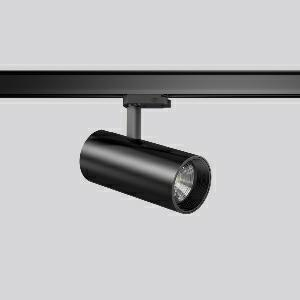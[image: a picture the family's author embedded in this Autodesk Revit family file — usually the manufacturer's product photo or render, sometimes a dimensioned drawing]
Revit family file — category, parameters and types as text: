
# Revit family: deecos_s_mini_742208_003_1_4eb7
name_source: partatom
category: Lighting Fixtures
units: mm (PartAtom-declared; Revit-internal decimal feet)

## family parameters
Cut with Voids When Loaded = No
Host = Face
Light Source = No
Part Type = Normal
Room Calculation Point = No
Round Connector Dimension = Use Diameter
Shared = No

## types (1)
- DEECOS S mini (1 x LED Modul 940, 3000 lm, 4000)
    Apparent Load = 29 VA
    Approval mark = CE
    CIE Flux Codes = 98 100 100 100 100
    Color Rendering = 92
    Color Temperature = 4000
    Default Elevation = 1800 mm
    Description = Series: DEECOS S mini
LED surface-mounted projector in modern design with no visible cooling ribs. Housing: die-cast aluminium, powder-coated. Rotation range: 356°. Swivel range: 90°. Black plastic ring and recessed LED to prevent glare from the side. Optical assembly with lens made of plastic (polycarbonate) for the best homogeneous light distribution - can be changed without tools. Best colour rendering index Ra>90. With multi adaptor for 3-circuit tracks 230 V. Suitable for Track on ceiling, Wall track. High quality converter without flickering and stroboscopic effect. The following accessories can be mounted without use of tools: interchangeable lenses, decorative glasses, honeycomb louvre, clear and frosted diffusers, white interchangeable plastic ring. 
Colour: deep black, matt (RAL 9005)
Diameter: 87 mm
Height: 214 mm
Lamp: LED
Socket: without socket
Colour temperature: 4000K
Colour rendering index (CRI): 92
System power: 29 W
Rated luminous flux: 3000 lm
Luminous efficiency: 103 lm/W
Control gear: Regulated power supply
Protection class: I
Type of protection: IP 20
    Height = 214 mm
    Lamp = 1 x LED Modul 940
    Lamp Light Flux = 3000 lm
    Lamp count = 1
    Length = 87 mm
    Lifetime = 50000 h
    Luminous efficacy = 103 lm/W
    Manufacturer = RZB
    ModVariant = No
    Model = 742208.003.1
    Mounting Place = Ceiling
    Mounting Type = Rail mounted
    Number of Poles = 1
    OnlyDefault = Yes
    Power Factor = 1
    Product Name = DEECOS S mini
    Product group = Track mounted projectors
    ProductGroupID = 301
    Protection Class = Protection class I
    Protection Degree = IP 20
    RLX_Detail_Level = 1
    RLX_Emergency_Light_Flux = 0 lm
    RLX_Emergency_Type = 0
    RLX_Emergency_Type_DB = No
    RlxData = <blob elided: 38793 chars, md5=b47558ec>
    Socket = socket
    Standby Power = 0 W
    System Light Flux = 3000 lm
    System Power = 29 W
    Type Comments = Product without accessories
    Type Image = 741930.003.jpg
    URL = http://relux.com
    VarID = ---
    Voltage = 230 V
    Voltage Range = 220-240 V
    Weight = 0.00 kg
    Width = 0 mm  [stored 0 ft]

note: [stored X ft] marks values corroborated as IEEE doubles in the binary element streams (Revit-internal decimal feet)

## geometry (parser evidence)
native form markers: Blend x4, Sweep x13
no freeform markers — native parametric forms only
